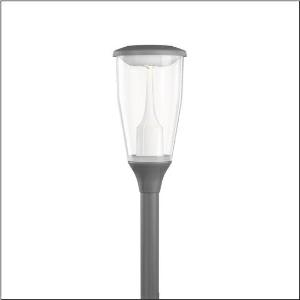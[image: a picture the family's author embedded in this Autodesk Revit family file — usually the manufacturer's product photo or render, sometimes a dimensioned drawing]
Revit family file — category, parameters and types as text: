
# Revit family: dl_11_iq___st1_2a_5xa5575ef14hp00022_53ae
name_source: partatom
category: Lighting Fixtures
units: mm (PartAtom-declared; Revit-internal decimal feet)

## family parameters
Cut with Voids When Loaded = No
Host = Face
Light Source = No
Part Type = Normal
Room Calculation Point = No
Round Connector Dimension = Use Diameter
Shared = No

## types (1)
- --- (1 x LED, 4840 lm, 33.6 W, 3000K)
    Apparent Load = 34 VA
    CIE Flux Codes = 33 63 91 94 100
    Color Rendering = 70
    Color Temperature = 3000K
    Default Elevation = 1800 mm
    Description = DL 11 iQ, mast luminaire, Module 540 iQ-SR, primary light control with 3 zone facetted reflector, of plastic, silver coated, highly specular, structured, primary optical cover: cover, of PMMA, transparent, light distribution: ST1.2a, light emission: direct distribution, primary light characteristic: asymmetric, installation type: post-top, LED, High Power LED, light colour: 730, colour temperature: 3000K, control: Street-Remote, Auto-Match, Temp-Guard, Lumen-Switch, Night-Set, Smart-Wire, Light-Fading, Desk-Remote (wireless, voltage-free reading and setting of iQ features in the workshop via application-optimized NFC function/RFID function), optimised constant luminous flux control (CLO 2.0), mains connection: 220..240V, AC, 50/60Hz, connection cable pre-assembled, cable length: 5,5m, luminaire housing, upper part, of diecast aluminium, coated, Siteco® metallic grey (DB 702S), spigot size: 76mm (post-top), post-top mast mounting element, of diecast aluminium, coated, Siteco® metallic grey (DB 702S), Module 540 iQ-SR, traffic white (RAL 9016), equipment: Power, protection rating (complete): IP66, insulation class (complete): insulation class II (safety insulation), certification: CE, ENEC, ENEC+, VDE, packaging unit: 1 piece

Light Distribution: ST1.2a
    Height = 665 mm
    Lamp = 1 x LED
    Lamp Light Flux = 4840 lm
    Lamp Power = 33.6 W
    Lamp count = 1
    Length = 334 mm
    Luminous efficacy = 144 lm/W
    Manufacturer = Siteco
    ModVariant = No
    Model = 5XA5575EF14HP00022
    Number of Poles = 1
    OnlyDefault = Yes
    Power Factor = 1
    Product Name = DL 11 iQ | ST1.2a
    Product group = mast luminaire | pylon top
    ProductGroupID = 6100
    Protection Class = Protection class II
    Protection Degree = IP 66
    RLX_Detail_Level = 1
    RLX_Emergency_Light_Flux = 0 lm
    RLX_Emergency_Type = 0
    RLX_Emergency_Type_DB = No
    RlxData = <blob elided: 155477 chars, md5=b44c88c1>
    Socket = socket
    Standby Power = 0 W
    System Light Flux = 4840 lm
    System Power = 34 W
    Type Comments = factory setting: luminous flux: 100 % | dim-lin: 254 | 695 mA
    Type Image = l_1258354.jpg
    URL = http://relux.com
    VarID = @adj_019921
    Voltage = 0 V
    Weight = 0.00 kg
    Width = 0 mm  [stored 0 ft]

note: [stored X ft] marks values corroborated as IEEE doubles in the binary element streams (Revit-internal decimal feet)

## geometry (parser evidence)
native form markers: Blend x4, Sweep x8
no freeform markers — native parametric forms only
